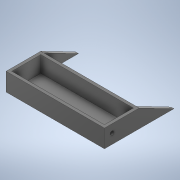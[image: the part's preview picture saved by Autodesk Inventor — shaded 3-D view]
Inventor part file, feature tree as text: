
AUTODESK INVENTOR PART (.ipt)
format: ipt  version: 2020 (Build 240168000, 168)  size: 209,920 bytes
history: native  units: in
note: dims shown in document units (in); Inventor stores cm internally (conversion verified against a paired STEP export)
features: extrude x4, sketch x4, mirror x2, projected_geometry x2
ambient origin geometry x8: Origin, YZ Plane, XZ Plane, XY Plane, X Axis, Y Axis, Z Axis, Center Point
bodies: Solid1 (feature_tree)
feature tree (12):
  extrude  "Extrusion1"  Depth=2.3622in
  extrude  "Extrusion2"  Depth=1.1024in TaperAngle=0.0deg
  extrude  "Extrusion7"  Depth=0.6693in
  mirror  "Mirror2"
  sketch  "Sketch14"  dims[d27=0.2756in d28=0.6693in]
  extrude  "Extrusion12"  Depth=0.1969in
  mirror  "Mirror5"
  sketch  "Sketch2"  dims[d0=6.6929in d1=2.3622in]
  projected_geometry  "Projected Loop1"
  sketch  "Sketch9"  dims[d2=0.1181in d3=0.0in d5=1.1024in d6=0.0in]
  sketch  "Sketch15"  dims[d30=0.4626in d31=0.0in d32=0.5906in d36=6.2992in d37=1.9685in d41=0.5118in d67=2.3622in d68=0.1969in d69=0.0in d50=0.0197in d51=0.0344in d52=0.0197in d53=0.0344in]
  projected_geometry  "Projected Loop6"
